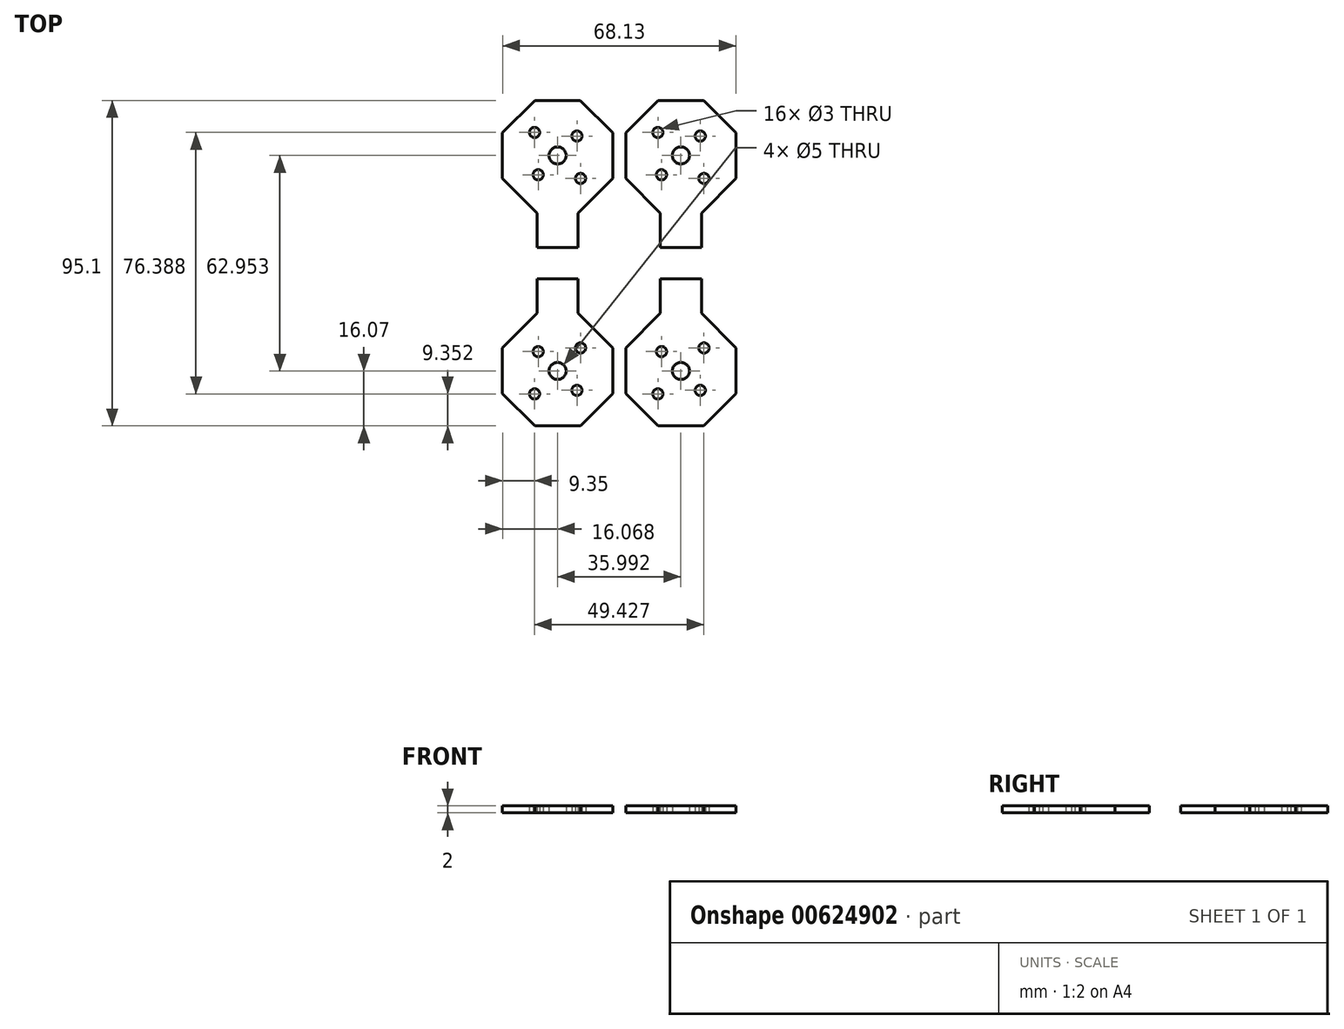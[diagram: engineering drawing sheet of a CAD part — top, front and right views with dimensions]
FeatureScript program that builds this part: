
annotation { "Feature Type Name" : "Feature", "Feature Type Description" : "" }
export const myFeature = defineFeature(function(context is Context, id is Id, definition is map)
    precondition{}
    {
        {
            var Q0;
            Q0=qCreatedBy(makeId("Top.planeOp"),FACE);
            var sketch = newSketch(context, id + "F0", { "sketchPlane" : qUnion([Q0])});
            skCircle(sketch, "E0", {"center": v(0, 0) * mm, "radius": 14 * mm, "construction": true});
            skLineSegment(sketch, "E1", {"start": v(9.9, 9.9) * mm, "end": v(0, 0) * mm, "construction": true});
            skLineSegment(sketch, "E2", {"start": v(0, 0) * mm, "end": v(-9.9, 9.9) * mm, "construction": true});
            skCircle(sketch, "E3", {"center": v(5.66, -5.66) * mm, "radius": 1.5 * mm});
            skCircle(sketch, "E4", {"center": v(-5.66, 5.66) * mm, "radius": 1.5 * mm});
            skLineSegment(sketch, "E5", {"start": v(0, 0) * mm, "end": v(-9.9, -9.9) * mm, "construction": true});
            skLineSegment(sketch, "E6", {"start": v(0, 0) * mm, "end": v(9.9, -9.9) * mm, "construction": true});
            skCircle(sketch, "E7", {"center": v(6.72, 6.72) * mm, "radius": 1.5 * mm});
            skCircle(sketch, "E8", {"center": v(-6.72, -6.72) * mm, "radius": 1.5 * mm});
            skCircle(sketch, "E9", {"center": v(0, 0) * mm, "radius": 2.5 * mm});
            skLineSegment(sketch, "E10.1", {"start": v(6, 16.93) * mm, "end": v(16.07, 6.66) * mm});
            skLineSegment(sketch, "E10.2", {"start": v(16.07, 6.66) * mm, "end": v(16.07, -6.66) * mm});
            skLineSegment(sketch, "E10.3", {"start": v(16.07, -6.66) * mm, "end": v(6.66, -16.07) * mm});
            skLineSegment(sketch, "E10.4", {"start": v(6.66, -16.07) * mm, "end": v(-6.66, -16.07) * mm});
            skLineSegment(sketch, "E10.5", {"start": v(-6.66, -16.07) * mm, "end": v(-16.07, -6.66) * mm});
            skLineSegment(sketch, "E10.6", {"start": v(-16.07, -6.66) * mm, "end": v(-16.07, 6.66) * mm});
            skLineSegment(sketch, "E10.7", {"start": v(-16.07, 6.66) * mm, "end": v(-6, 16.93) * mm});
            skLineSegment(sketch, "E11", {"start": v(6, 16.93) * mm, "end": v(6, 26.93) * mm});
            skLineSegment(sketch, "E12", {"start": v(6, 26.93) * mm, "end": v(-6, 26.93) * mm});
            skLineSegment(sketch, "E13", {"start": v(-6, 26.93) * mm, "end": v(-6, 16.93) * mm});
            skCircle(sketch, "E14", {"center": v(-36, 0) * mm, "radius": 14 * mm, "construction": true});
            skLineSegment(sketch, "E15", {"start": v(-26.1, 9.9) * mm, "end": v(-36, 0) * mm, "construction": true});
            skLineSegment(sketch, "E16", {"start": v(-36, 0) * mm, "end": v(-45.9, 9.9) * mm, "construction": true});
            skCircle(sketch, "E17", {"center": v(-30.34, -5.66) * mm, "radius": 1.5 * mm});
            skCircle(sketch, "E18", {"center": v(-41.65, 5.66) * mm, "radius": 1.5 * mm});
            skLineSegment(sketch, "E19", {"start": v(-36, 0) * mm, "end": v(-45.9, -9.9) * mm, "construction": true});
            skLineSegment(sketch, "E20", {"start": v(-36, 0) * mm, "end": v(-26.1, -9.9) * mm, "construction": true});
            skCircle(sketch, "E21", {"center": v(-29.27, 6.72) * mm, "radius": 1.5 * mm});
            skCircle(sketch, "E22", {"center": v(-42.7, -6.72) * mm, "radius": 1.5 * mm});
            skCircle(sketch, "E23", {"center": v(-36, 0) * mm, "radius": 2.5 * mm});
            skLineSegment(sketch, "E24.1", {"start": v(-30, 16.93) * mm, "end": v(-19.9, 6.68) * mm});
            skLineSegment(sketch, "E24.2", {"start": v(-19.9, 6.68) * mm, "end": v(-19.9, -6.64) * mm});
            skLineSegment(sketch, "E24.3", {"start": v(-19.9, -6.64) * mm, "end": v(-29.31, -16.05) * mm});
            skLineSegment(sketch, "E24.4", {"start": v(-29.31, -16.05) * mm, "end": v(-42.65, -16.07) * mm});
            skLineSegment(sketch, "E24.5", {"start": v(-42.65, -16.07) * mm, "end": v(-52.06, -6.66) * mm});
            skLineSegment(sketch, "E24.6", {"start": v(-52.06, -6.66) * mm, "end": v(-52.06, 6.66) * mm});
            skLineSegment(sketch, "E24.7", {"start": v(-52.06, 6.66) * mm, "end": v(-42, 16.93) * mm});
            skLineSegment(sketch, "E25", {"start": v(-30, 16.93) * mm, "end": v(-30, 26.93) * mm});
            skLineSegment(sketch, "E26", {"start": v(-30, 26.93) * mm, "end": v(-42, 26.93) * mm});
            skLineSegment(sketch, "E27", {"start": v(-42, 26.93) * mm, "end": v(-42, 16.93) * mm});
            skCircle(sketch, "E28.MirrorC", {"center": v(5.66, 68.61) * mm, "radius": 1.5 * mm});
            skCircle(sketch, "E29.MirrorC", {"center": v(-5.66, 57.3) * mm, "radius": 1.5 * mm});
            skCircle(sketch, "E30.MirrorC", {"center": v(6.72, 56.24) * mm, "radius": 1.5 * mm});
            skCircle(sketch, "E31.MirrorC", {"center": v(-29.27, 56.24) * mm, "radius": 1.5 * mm});
            skLineSegment(sketch, "E32.MirrorCS", {"start": v(-36, 62.95) * mm, "end": v(-45.9, 53.05) * mm, "construction": true});
            skLineSegment(sketch, "E33.MirrorCS", {"start": v(0, 62.95) * mm, "end": v(-9.9, 53.05) * mm, "construction": true});
            skCircle(sketch, "E34.MirrorC", {"center": v(-6.72, 69.67) * mm, "radius": 1.5 * mm});
            skCircle(sketch, "E35.MirrorC", {"center": v(-41.65, 57.3) * mm, "radius": 1.5 * mm});
            skCircle(sketch, "E36.MirrorC", {"center": v(-42.7, 69.67) * mm, "radius": 1.5 * mm});
            skCircle(sketch, "E37.MirrorC", {"center": v(-30.34, 68.61) * mm, "radius": 1.5 * mm});
            skLineSegment(sketch, "E38.MirrorCS", {"start": v(0, 62.95) * mm, "end": v(9.9, 72.85) * mm, "construction": true});
            skLineSegment(sketch, "E39.MirrorCS", {"start": v(-42, 36.03) * mm, "end": v(-42, 46.03) * mm});
            skCircle(sketch, "E40.MirrorC", {"center": v(0, 62.95) * mm, "radius": 2.5 * mm});
            skLineSegment(sketch, "E41.MirrorCS", {"start": v(6, 46.03) * mm, "end": v(16.07, 56.3) * mm});
            skLineSegment(sketch, "E42.MirrorCS", {"start": v(-30, 46.07) * mm, "end": v(-30, 36.03) * mm});
            skLineSegment(sketch, "E43.MirrorCS", {"start": v(-30, 46.07) * mm, "end": v(-19.92, 56.3) * mm});
            skLineSegment(sketch, "E44.MirrorCS", {"start": v(-42.65, 79.03) * mm, "end": v(-52.06, 69.61) * mm});
            skLineSegment(sketch, "E45.MirrorCS", {"start": v(-36, 62.95) * mm, "end": v(-45.9, 72.85) * mm, "construction": true});
            skLineSegment(sketch, "E46.MirrorCS", {"start": v(-30, 36.03) * mm, "end": v(-42, 36.03) * mm});
            skLineSegment(sketch, "E47.MirrorCS", {"start": v(-19.92, 56.3) * mm, "end": v(-19.92, 69.61) * mm});
            skLineSegment(sketch, "E48.MirrorCS", {"start": v(6, 36.07) * mm, "end": v(-6, 36.07) * mm});
            skLineSegment(sketch, "E49.MirrorCS", {"start": v(9.9, 53.05) * mm, "end": v(0, 62.95) * mm, "construction": true});
            skCircle(sketch, "E50.MirrorC", {"center": v(0, 62.95) * mm, "radius": 14 * mm, "construction": true});
            skLineSegment(sketch, "E51.MirrorCS", {"start": v(16.07, 69.61) * mm, "end": v(6.66, 79.03) * mm});
            skLineSegment(sketch, "E52.MirrorCS", {"start": v(16.07, 56.3) * mm, "end": v(16.07, 69.61) * mm});
            skLineSegment(sketch, "E53.MirrorCS", {"start": v(0, 62.95) * mm, "end": v(-9.9, 72.85) * mm, "construction": true});
            skLineSegment(sketch, "E54.MirrorCS", {"start": v(-16.07, 69.61) * mm, "end": v(-16.07, 56.3) * mm});
            skLineSegment(sketch, "E55.MirrorCS", {"start": v(-6.66, 79.03) * mm, "end": v(-16.07, 69.61) * mm});
            skLineSegment(sketch, "E56.MirrorCS", {"start": v(6.66, 79.03) * mm, "end": v(-6.66, 79.03) * mm});
            skLineSegment(sketch, "E57.MirrorCS", {"start": v(-52.06, 69.61) * mm, "end": v(-52.06, 56.3) * mm});
            skLineSegment(sketch, "E58.MirrorCS", {"start": v(-6, 36.07) * mm, "end": v(-6, 46.07) * mm});
            skLineSegment(sketch, "E59.MirrorCS", {"start": v(-36, 62.95) * mm, "end": v(-26.1, 72.85) * mm, "construction": true});
            skLineSegment(sketch, "E60.MirrorCS", {"start": v(-29.33, 79.03) * mm, "end": v(-42.65, 79.03) * mm});
            skLineSegment(sketch, "E61.MirrorCS", {"start": v(6, 46.03) * mm, "end": v(6, 36.07) * mm});
            skLineSegment(sketch, "E62.MirrorCS", {"start": v(-26.1, 53.05) * mm, "end": v(-36, 62.95) * mm, "construction": true});
            skLineSegment(sketch, "E63.MirrorCS", {"start": v(-19.92, 69.61) * mm, "end": v(-29.33, 79.03) * mm});
            skLineSegment(sketch, "E64.MirrorCS", {"start": v(-16.07, 56.3) * mm, "end": v(-6, 46.07) * mm});
            skLineSegment(sketch, "E65.MirrorCS", {"start": v(-52.06, 56.3) * mm, "end": v(-42, 46.03) * mm});
            skCircle(sketch, "E66.MirrorC", {"center": v(-36, 62.95) * mm, "radius": 2.5 * mm});
            skCircle(sketch, "E67.MirrorC", {"center": v(-36, 62.95) * mm, "radius": 14 * mm, "construction": true});
            skSolve(sketch);
        }
        {
            var Q0;
            Q0 = qSketchRegion(id + "F0", true);
            extrude(context, id + "F1", {"entities" : qUnion([Q0]), "depth" : 2 * mm, "offsetDistance" : 25 * mm});
        }
    });
